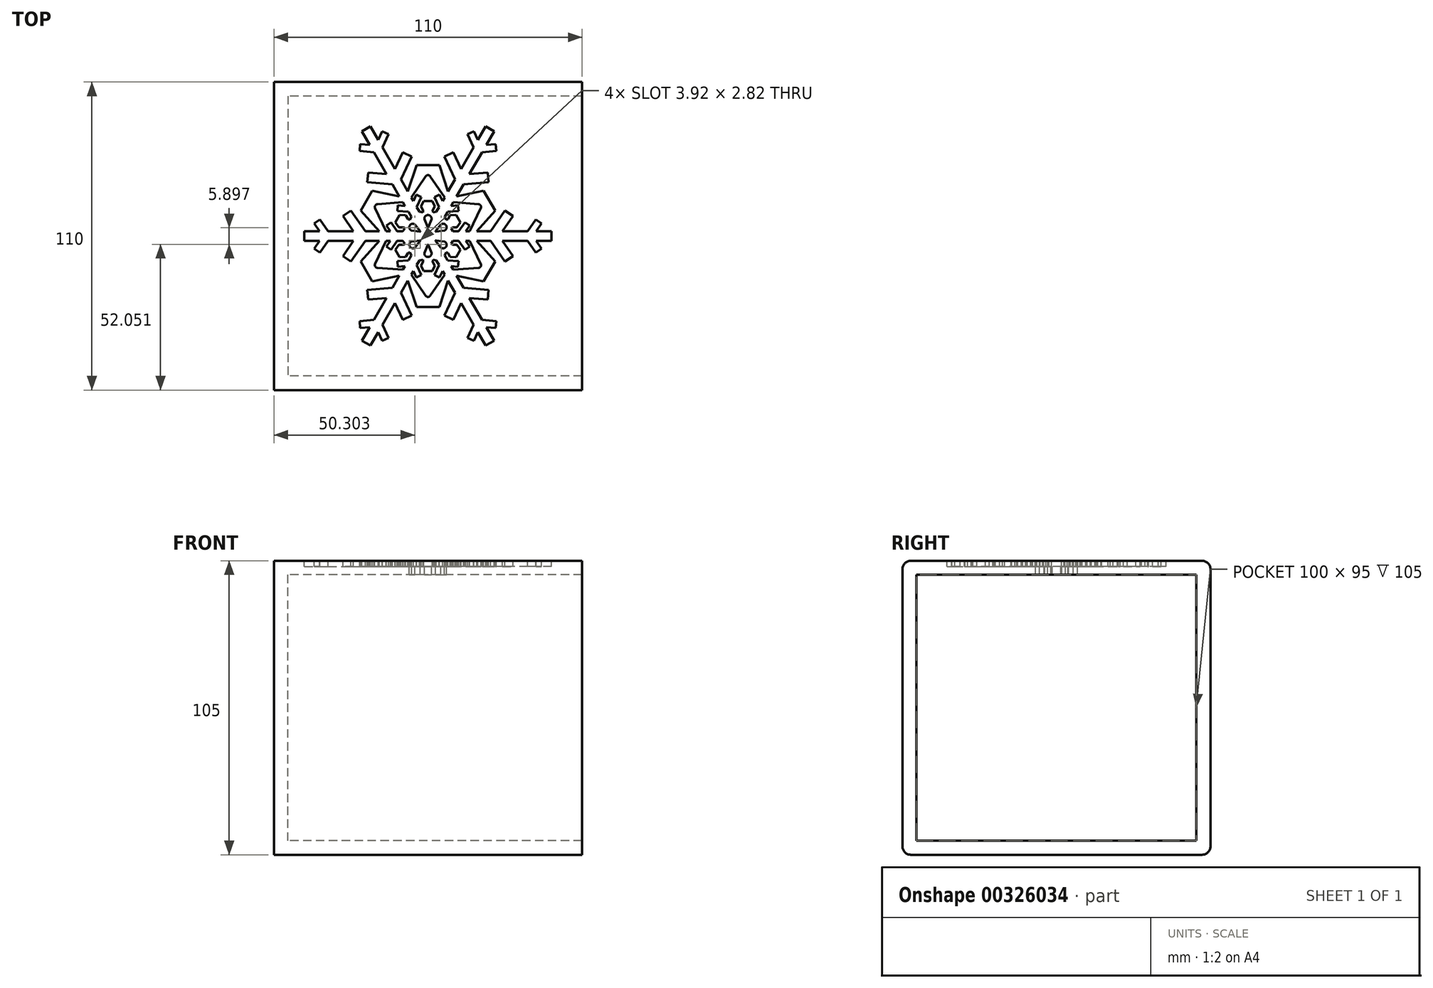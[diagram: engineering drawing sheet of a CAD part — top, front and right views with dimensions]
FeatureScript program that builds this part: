
annotation { "Feature Type Name" : "Feature", "Feature Type Description" : "" }
export const myFeature = defineFeature(function(context is Context, id is Id, definition is map)
    precondition{}
    {
        {
            var Q0;
            Q0=qCreatedBy(makeId("Top.planeOp"),FACE);
            var sketch = newSketch(context, id + "F0", { "sketchPlane" : qUnion([Q0])});
            skLineSegment(sketch, "E0.bottom", {"start": v(-43.7, 44.8) * mm, "end": v(41.1, 44.8) * mm});
            skLineSegment(sketch, "E0.top", {"start": v(-43.7, -40) * mm, "end": v(41.1, -40) * mm});
            skLineSegment(sketch, "E0.left", {"start": v(-43.7, 44.8) * mm, "end": v(-43.7, -40) * mm});
            skLineSegment(sketch, "E0.right", {"start": v(41.1, 44.8) * mm, "end": v(41.1, -40) * mm});
            skLineSegment(sketch, "E1", {"start": v(-44.15, 0) * mm, "end": v(-44.15, 1.75) * mm});
            skLineSegment(sketch, "E2", {"start": v(-44.15, 1.75) * mm, "end": v(-38.65, 1.75) * mm});
            skLineSegment(sketch, "E3", {"start": v(-38.65, 1.75) * mm, "end": v(-40.58, 4.5) * mm});
            skLineSegment(sketch, "E4", {"start": v(-40.58, 4.5) * mm, "end": v(-38.53, 5.94) * mm});
            skLineSegment(sketch, "E5", {"start": v(-38.53, 5.94) * mm, "end": v(-35.6, 1.75) * mm});
            skLineSegment(sketch, "E6", {"start": v(-35.6, 1.75) * mm, "end": v(-26.6, 1.75) * mm});
            skLineSegment(sketch, "E7", {"start": v(-26.6, 1.75) * mm, "end": v(-30.36, 7.13) * mm});
            skLineSegment(sketch, "E8", {"start": v(-30.36, 7.13) * mm, "end": v(-27.49, 9.13) * mm});
            skLineSegment(sketch, "E9", {"start": v(-27.49, 9.13) * mm, "end": v(-22.34, 1.75) * mm});
            skLineSegment(sketch, "E10", {"start": v(-22.34, 1.75) * mm, "end": v(-17.4, 1.75) * mm});
            skLineSegment(sketch, "E11", {"start": v(-14.94, 1.75) * mm, "end": v(-13.44, 1.75) * mm});
            skLineSegment(sketch, "E12", {"start": v(-13.44, 1.75) * mm, "end": v(-14.87, 3.8) * mm});
            skLineSegment(sketch, "E13", {"start": v(-14.87, 3.8) * mm, "end": v(-13.23, 4.94) * mm});
            skLineSegment(sketch, "E14", {"start": v(-13.23, 4.94) * mm, "end": v(-11, 1.75) * mm});
            skLineSegment(sketch, "E15", {"start": v(0, 0) * mm, "end": v(-44.15, 0) * mm, "construction": true});
            skLineSegment(sketch, "E16", {"start": v(-11, 1.75) * mm, "end": v(-8.98, 1.75) * mm});
            skLineSegment(sketch, "E17", {"start": v(0, 0) * mm, "end": v(-10.85, 6.27) * mm});
            skLineSegment(sketch, "E18", {"start": v(-8.98, 1.75) * mm, "end": v(-8.24, 2.67) * mm});
            skLineSegment(sketch, "E19", {"start": v(-8.24, 2.67) * mm, "end": v(-8.84, 3.15) * mm});
            skLineSegment(sketch, "E20", {"start": v(-8.84, 3.15) * mm, "end": v(-10.37, 3.15) * mm});
            skLineSegment(sketch, "E21", {"start": v(-10.37, 3.15) * mm, "end": v(-11.62, 4.94) * mm});
            skLineSegment(sketch, "E22", {"start": v(-11.62, 4.94) * mm, "end": v(-10.85, 6.27) * mm});
            skLineSegment(sketch, "E23", {"start": v(-10.85, 6.27) * mm, "end": v(-31.84, 18.38) * mm, "construction": true});
            skLineSegment(sketch, "E24", {"start": v(-23.98, 9.13) * mm, "end": v(-21.94, 12.67) * mm});
            skLineSegment(sketch, "E25", {"start": v(-14.94, 1.75) * mm, "end": v(-19.5, 11.26) * mm});
            skLineSegment(sketch, "E26", {"start": v(-23.98, 9.13) * mm, "end": v(-17.4, 1.75) * mm});
            skLineSegment(sketch, "E27", {"start": v(-21.94, 12.67) * mm, "end": v(-19.5, 11.26) * mm});
            skLineSegment(sketch, "E28.MirrorCS", {"start": v(0, 0) * mm, "end": v(-10.85, -6.27) * mm});
            skLineSegment(sketch, "E29.MirrorCS", {"start": v(-44.15, 0) * mm, "end": v(-44.15, -1.75) * mm});
            skLineSegment(sketch, "E30.MirrorCS", {"start": v(-14.94, -1.75) * mm, "end": v(-13.44, -1.75) * mm});
            skLineSegment(sketch, "E31.MirrorCS", {"start": v(-11.62, -4.94) * mm, "end": v(-10.85, -6.27) * mm});
            skLineSegment(sketch, "E32.MirrorCS", {"start": v(-14.87, -3.8) * mm, "end": v(-13.23, -4.94) * mm});
            skLineSegment(sketch, "E33.MirrorCS", {"start": v(-8.98, -1.75) * mm, "end": v(-8.24, -2.67) * mm});
            skLineSegment(sketch, "E34.MirrorCS", {"start": v(-8.84, -3.15) * mm, "end": v(-10.37, -3.15) * mm});
            skLineSegment(sketch, "E35.MirrorCS", {"start": v(-8.24, -2.67) * mm, "end": v(-8.84, -3.15) * mm});
            skLineSegment(sketch, "E36.MirrorCS", {"start": v(-14.94, -1.75) * mm, "end": v(-19.5, -11.26) * mm});
            skLineSegment(sketch, "E37.MirrorCS", {"start": v(-27.49, -9.13) * mm, "end": v(-22.34, -1.75) * mm});
            skLineSegment(sketch, "E38.MirrorCS", {"start": v(-21.94, -12.67) * mm, "end": v(-19.5, -11.26) * mm});
            skLineSegment(sketch, "E39.MirrorCS", {"start": v(-23.98, -9.13) * mm, "end": v(-21.94, -12.67) * mm});
            skLineSegment(sketch, "E40.MirrorCS", {"start": v(-11, -1.75) * mm, "end": v(-8.98, -1.75) * mm});
            skLineSegment(sketch, "E41.MirrorCS", {"start": v(-38.53, -5.94) * mm, "end": v(-35.6, -1.75) * mm});
            skLineSegment(sketch, "E42.MirrorCS", {"start": v(-40.58, -4.5) * mm, "end": v(-38.53, -5.94) * mm});
            skLineSegment(sketch, "E43.MirrorCS", {"start": v(-38.65, -1.75) * mm, "end": v(-40.58, -4.5) * mm});
            skLineSegment(sketch, "E44.MirrorCS", {"start": v(-44.15, -1.75) * mm, "end": v(-38.65, -1.75) * mm});
            skLineSegment(sketch, "E45.MirrorCS", {"start": v(-23.98, -9.13) * mm, "end": v(-17.4, -1.75) * mm});
            skLineSegment(sketch, "E46.MirrorCS", {"start": v(-30.36, -7.13) * mm, "end": v(-27.49, -9.13) * mm});
            skLineSegment(sketch, "E47.MirrorCS", {"start": v(-26.6, -1.75) * mm, "end": v(-30.36, -7.13) * mm});
            skLineSegment(sketch, "E48.MirrorCS", {"start": v(-35.6, -1.75) * mm, "end": v(-26.6, -1.75) * mm});
            skLineSegment(sketch, "E49.MirrorCS", {"start": v(-22.34, -1.75) * mm, "end": v(-17.4, -1.75) * mm});
            skLineSegment(sketch, "E50.MirrorCS", {"start": v(-13.44, -1.75) * mm, "end": v(-14.87, -3.8) * mm});
            skLineSegment(sketch, "E51.MirrorCS", {"start": v(-10.37, -3.15) * mm, "end": v(-11.62, -4.94) * mm});
            skLineSegment(sketch, "E52.MirrorCS", {"start": v(-13.23, -4.94) * mm, "end": v(-11, -1.75) * mm});
            skSolve(sketch);
        }
        {
            var Q0;
            Q0=makeQuery(id+"F0.imprint","IMPRINT",FACE,{"disambiguationData":[TD([[makeQuery(id+"F0.imprint","IMPRINT",EDGE,{"derivedFrom":sQuery(id+"F0.wireOp",EDGE,"E1")}),-1.0]])]});
            var Q1;
            {var subQ0=sQuery(id+"F0.wireOp",EDGE,"E3");Q1=makeQuery(id+"F0.imprint","IMPRINT",FACE,{"disambiguationData":[TD([[makeQuery(id+"F0.imprint","IMPRINT",EDGE,{"derivedFrom":subQ0}),-1.0]])]});}
            extrude(context, id + "F1", {"entities" : qUnion([Q0, Q1]), "endBound" : BoundingType.SYMMETRIC, "depth" : 3 * mm});
        }
        {
            var Q0;
            Q0=qCreatedBy(makeId("Right.planeOp"),FACE);
            var sketch = newSketch(context, id + "F2", { "sketchPlane" : qUnion([Q0])});
            skLineSegment(sketch, "E53", {"start": v(0, 0) * mm, "end": v(0, -43.45) * mm, "construction": true});
            skSolve(sketch);
        }
        {
            var Q0;
            Q0=makeQuery(id+"F1.opExtrude","SWEPT_BODY",BODY,{"disambiguationData":[OSD([sQuery(id+"F0.wireOp",EDGE,"E1"),sQuery(id+"F0.wireOp",EDGE,"E2"),sQuery(id+"F0.wireOp",EDGE,"E3"),sQuery(id+"F0.wireOp",EDGE,"E4"),sQuery(id+"F0.wireOp",EDGE,"E5"),sQuery(id+"F0.wireOp",EDGE,"E6"),sQuery(id+"F0.wireOp",EDGE,"E7"),sQuery(id+"F0.wireOp",EDGE,"E8"),sQuery(id+"F0.wireOp",EDGE,"E9"),sQuery(id+"F0.wireOp",EDGE,"E10"),sQuery(id+"F0.wireOp",EDGE,"189a7a4e-f39c-4bfd-b122-43a29ca94680"),sQuery(id+"F0.wireOp",EDGE,"67050dc1-3990-4a49-9707-dffdccfb30a0"),sQuery(id+"F0.wireOp",EDGE,"437a0215-fb6c-4063-ad75-b84b83856d58"),sQuery(id+"F0.wireOp",EDGE,"E11"),sQuery(id+"F0.wireOp",EDGE,"E12"),sQuery(id+"F0.wireOp",EDGE,"E13"),sQuery(id+"F0.wireOp",EDGE,"E14"),sQuery(id+"F0.wireOp",EDGE,"5e9898c1-a996-4e9f-834a-20b7154747a1"),sQuery(id+"F0.wireOp",EDGE,"4f175b08-8b9f-4015-be58-81c3dce13333"),sQuery(id+"F0.wireOp",EDGE,"3166d6ec-2b74-46b0-8a25-8ff819b97b050.MirrorCS"),sQuery(id+"F0.wireOp",EDGE,"3166d6ec-2b74-46b0-8a25-8ff819b97b051.MirrorCS"),sQuery(id+"F0.wireOp",EDGE,"3166d6ec-2b74-46b0-8a25-8ff819b97b052.MirrorCS"),sQuery(id+"F0.wireOp",EDGE,"3166d6ec-2b74-46b0-8a25-8ff819b97b053.MirrorCS"),sQuery(id+"F0.wireOp",EDGE,"3166d6ec-2b74-46b0-8a25-8ff819b97b054.MirrorCS"),sQuery(id+"F0.wireOp",EDGE,"3166d6ec-2b74-46b0-8a25-8ff819b97b055.MirrorCS"),sQuery(id+"F0.wireOp",EDGE,"3166d6ec-2b74-46b0-8a25-8ff819b97b056.MirrorCS"),sQuery(id+"F0.wireOp",EDGE,"3166d6ec-2b74-46b0-8a25-8ff819b97b057.MirrorCS"),sQuery(id+"F0.wireOp",EDGE,"3166d6ec-2b74-46b0-8a25-8ff819b97b058.MirrorCS"),sQuery(id+"F0.wireOp",EDGE,"3166d6ec-2b74-46b0-8a25-8ff819b97b059.MirrorCS"),sQuery(id+"F0.wireOp",EDGE,"3166d6ec-2b74-46b0-8a25-8ff819b97b0510.MirrorCS"),sQuery(id+"F0.wireOp",EDGE,"3166d6ec-2b74-46b0-8a25-8ff819b97b0511.MirrorCS"),sQuery(id+"F0.wireOp",EDGE,"3166d6ec-2b74-46b0-8a25-8ff819b97b0512.MirrorCS"),sQuery(id+"F0.wireOp",EDGE,"3166d6ec-2b74-46b0-8a25-8ff819b97b0513.MirrorCS"),sQuery(id+"F0.wireOp",EDGE,"3166d6ec-2b74-46b0-8a25-8ff819b97b0514.MirrorCS"),sQuery(id+"F0.wireOp",EDGE,"3166d6ec-2b74-46b0-8a25-8ff819b97b0515.MirrorCS"),sQuery(id+"F0.wireOp",EDGE,"3166d6ec-2b74-46b0-8a25-8ff819b97b0516.MirrorCS"),sQuery(id+"F0.wireOp",EDGE,"3166d6ec-2b74-46b0-8a25-8ff819b97b0517.MirrorCS"),sQuery(id+"F0.wireOp",EDGE,"3166d6ec-2b74-46b0-8a25-8ff819b97b0518.MirrorCS")])]});
            var Q1;
            Q1=sQuery(id+"F2.wireOp",EDGE,"E53");
            circularPattern(context, id + "F3", {"operationType" : NewBodyOperationType.ADD, "entities" : qUnion([Q0]), "axis" : qUnion([Q1]), "angle" : 60 * degree, "instanceCount" : 6});
        }
        {
            var Q0;
            {var subQ0=makeQuery(id+"F1.opExtrude","CAP_FACE",FACE,{"disambiguationData":[OSD([sQuery(id+"F0.wireOp",EDGE,"E1"),sQuery(id+"F0.wireOp",EDGE,"E2"),sQuery(id+"F0.wireOp",EDGE,"E3"),sQuery(id+"F0.wireOp",EDGE,"E4"),sQuery(id+"F0.wireOp",EDGE,"E5"),sQuery(id+"F0.wireOp",EDGE,"E6"),sQuery(id+"F0.wireOp",EDGE,"E7"),sQuery(id+"F0.wireOp",EDGE,"E8"),sQuery(id+"F0.wireOp",EDGE,"E9"),sQuery(id+"F0.wireOp",EDGE,"E10"),sQuery(id+"F0.wireOp",EDGE,"189a7a4e-f39c-4bfd-b122-43a29ca94680"),sQuery(id+"F0.wireOp",EDGE,"67050dc1-3990-4a49-9707-dffdccfb30a0"),sQuery(id+"F0.wireOp",EDGE,"437a0215-fb6c-4063-ad75-b84b83856d58"),sQuery(id+"F0.wireOp",EDGE,"E11"),sQuery(id+"F0.wireOp",EDGE,"E12"),sQuery(id+"F0.wireOp",EDGE,"E13"),sQuery(id+"F0.wireOp",EDGE,"E14"),sQuery(id+"F0.wireOp",EDGE,"E16"),sQuery(id+"F0.wireOp",EDGE,"E17"),sQuery(id+"F0.wireOp",EDGE,"E18"),sQuery(id+"F0.wireOp",EDGE,"E19"),sQuery(id+"F0.wireOp",EDGE,"E20"),sQuery(id+"F0.wireOp",EDGE,"E21"),sQuery(id+"F0.wireOp",EDGE,"E22"),sQuery(id+"F0.wireOp",EDGE,"0c32c283-354d-45ec-8926-575daeb4bd260.MirrorCS"),sQuery(id+"F0.wireOp",EDGE,"0c32c283-354d-45ec-8926-575daeb4bd261.MirrorCS"),sQuery(id+"F0.wireOp",EDGE,"0c32c283-354d-45ec-8926-575daeb4bd262.MirrorCS"),sQuery(id+"F0.wireOp",EDGE,"0c32c283-354d-45ec-8926-575daeb4bd263.MirrorCS"),sQuery(id+"F0.wireOp",EDGE,"0c32c283-354d-45ec-8926-575daeb4bd264.MirrorCS"),sQuery(id+"F0.wireOp",EDGE,"0c32c283-354d-45ec-8926-575daeb4bd265.MirrorCS"),sQuery(id+"F0.wireOp",EDGE,"0c32c283-354d-45ec-8926-575daeb4bd266.MirrorCS"),sQuery(id+"F0.wireOp",EDGE,"0c32c283-354d-45ec-8926-575daeb4bd267.MirrorCS"),sQuery(id+"F0.wireOp",EDGE,"0c32c283-354d-45ec-8926-575daeb4bd268.MirrorCS"),sQuery(id+"F0.wireOp",EDGE,"0c32c283-354d-45ec-8926-575daeb4bd269.MirrorCS"),sQuery(id+"F0.wireOp",EDGE,"0c32c283-354d-45ec-8926-575daeb4bd2610.MirrorCS"),sQuery(id+"F0.wireOp",EDGE,"0c32c283-354d-45ec-8926-575daeb4bd2611.MirrorCS"),sQuery(id+"F0.wireOp",EDGE,"0c32c283-354d-45ec-8926-575daeb4bd2612.MirrorCS"),sQuery(id+"F0.wireOp",EDGE,"0c32c283-354d-45ec-8926-575daeb4bd2613.MirrorCS"),sQuery(id+"F0.wireOp",EDGE,"0c32c283-354d-45ec-8926-575daeb4bd2614.MirrorCS"),sQuery(id+"F0.wireOp",EDGE,"0c32c283-354d-45ec-8926-575daeb4bd2615.MirrorCS"),sQuery(id+"F0.wireOp",EDGE,"0c32c283-354d-45ec-8926-575daeb4bd2616.MirrorCS"),sQuery(id+"F0.wireOp",EDGE,"0c32c283-354d-45ec-8926-575daeb4bd2617.MirrorCS"),sQuery(id+"F0.wireOp",EDGE,"0c32c283-354d-45ec-8926-575daeb4bd2618.MirrorCS"),sQuery(id+"F0.wireOp",EDGE,"0c32c283-354d-45ec-8926-575daeb4bd2619.MirrorCS"),sQuery(id+"F0.wireOp",EDGE,"0c32c283-354d-45ec-8926-575daeb4bd2620.MirrorCS"),sQuery(id+"F0.wireOp",EDGE,"0c32c283-354d-45ec-8926-575daeb4bd2621.MirrorCS"),sQuery(id+"F0.wireOp",EDGE,"0c32c283-354d-45ec-8926-575daeb4bd2622.MirrorCS"),sQuery(id+"F0.wireOp",EDGE,"0c32c283-354d-45ec-8926-575daeb4bd2623.MirrorCS")])],"isStart":false});Q0=makeQuery(id+"F3.boolean.opBoolean","MERGE",FACE,{"derivedFrom":[subQ0,makeQuery(id+"F3.opPattern","COPY",FACE,{"derivedFrom":subQ0,"instanceName":"1"}),makeQuery(id+"F3.opPattern","COPY",FACE,{"derivedFrom":subQ0,"instanceName":"2"}),makeQuery(id+"F3.opPattern","COPY",FACE,{"derivedFrom":subQ0,"instanceName":"3"}),makeQuery(id+"F3.opPattern","COPY",FACE,{"derivedFrom":subQ0,"instanceName":"4"}),makeQuery(id+"F3.opPattern","COPY",FACE,{"derivedFrom":subQ0,"instanceName":"5"})]});}
            var sketch = newSketch(context, id + "F4", { "sketchPlane" : qUnion([Q0])});
            skLineSegment(sketch, "E54", {"start": v(0, 0) * mm, "end": v(-10.85, 6.27) * mm, "construction": true});
            skLineSegment(sketch, "E55", {"start": v(-6.5, 3.75) * mm, "end": v(-2.6, 1.5) * mm, "construction": true});
            skLineSegment(sketch, "E56", {"start": v(-5.87, 1.94) * mm, "end": v(-2.6, 1.5) * mm});
            skLineSegment(sketch, "E57.MirrorCS", {"start": v(-4.62, 4.1) * mm, "end": v(-2.6, 1.5) * mm});
            skLineSegment(sketch, "E58", {"start": v(-5.87, 1.94) * mm, "end": v(-4.62, 4.1) * mm, "construction": true});
            skArc(sketch, "E59", {"start": v(-4.62, 4.1) * mm, "mid": v(-6.5, 3.75) * mm, "end": v(-5.87, 1.94) * mm});
            skSolve(sketch);
        }
        {
            var Q0;
            Q0=makeQuery(id+"F4.imprint","IMPRINT",FACE,{"disambiguationData":[TD([[makeQuery(id+"F4.imprint","IMPRINT",EDGE,{"derivedFrom":sQuery(id+"F4.wireOp",EDGE,"980073ca-cf30-472a-b92e-9ee7ff5da41c")}),1.0]])]});
            var Q1;
            Q1=makeQuery(id+"F4.imprint","IMPRINT",FACE,{"disambiguationData":[TD([[makeQuery(id+"F4.imprint","IMPRINT",EDGE,{"derivedFrom":sQuery(id+"F4.wireOp",EDGE,"E56")}),1.0]])]});
            extrude(context, id + "F5", {"entities" : qUnion([Q0, Q1]), "operationType" : NewBodyOperationType.REMOVE, "endBound" : BoundingType.UP_TO_NEXT, "oppositeDirection" : true, "depth" : 25 * mm});
        }
        {
            var Q0;
            Q0=makeQuery(id+"F5.boolean.opBoolean","COPY",EDGE,{"derivedFrom":makeQuery(id+"F5.opExtrude","SWEPT_EDGE",EDGE,{"disambiguationData":[OSD([sQuery(id+"F4.wireOp",EDGE,"E56"),sQuery(id+"F4.wireOp",EDGE,"E57.MirrorCS")])]})});
            fillet(context, id + "F6", {"entities" : qUnion([Q0]), "radius" : 0.1 * mm, "tangentPropagation" : true, "allowEdgeOverflow" : false});
        }
        {
            var Q0;
            Q0=makeQuery(id+"F5.boolean.opBoolean","COPY",FACE,{"derivedFrom":makeQuery(id+"F5.opExtrude","SWEPT_FACE",FACE,{"disambiguationData":[OSD([sQuery(id+"F4.wireOp",EDGE,"E59")])]})});
            var Q1;
            Q1=makeQuery(id+"F5.boolean.opBoolean","COPY",FACE,{"derivedFrom":makeQuery(id+"F5.opExtrude","SWEPT_FACE",FACE,{"disambiguationData":[OSD([sQuery(id+"F4.wireOp",EDGE,"E56")])]})});
            var Q2;
            Q2=makeQuery(id+"F5.boolean.opBoolean","COPY",FACE,{"derivedFrom":makeQuery(id+"F5.opExtrude","SWEPT_FACE",FACE,{"disambiguationData":[OSD([sQuery(id+"F4.wireOp",EDGE,"E57.MirrorCS")])]})});
            var Q3;
            Q3=makeQuery(id+"F6.opFillet","BLEND_FACE",FACE,{"disambiguationData":[OSD([sQuery(id+"F4.wireOp",EDGE,"E56"),sQuery(id+"F4.wireOp",EDGE,"E57.MirrorCS")])]});
            var Q4;
            Q4=sQuery(id+"F2.wireOp",EDGE,"E53");
            circularPattern(context, id + "F7", {"faces" : qUnion([Q0, Q1, Q2, Q3]), "axis" : qUnion([Q4]), "angle" : 60 * degree, "instanceCount" : 6, "patternType" : PatternType.FACE});
        }
        {
            var Q0;
            {var subQ0=makeQuery(id+"F1.opExtrude","CAP_FACE",FACE,{"disambiguationData":[OSD([sQuery(id+"F0.wireOp",EDGE,"E1"),sQuery(id+"F0.wireOp",EDGE,"E2"),sQuery(id+"F0.wireOp",EDGE,"E3"),sQuery(id+"F0.wireOp",EDGE,"E4"),sQuery(id+"F0.wireOp",EDGE,"E5"),sQuery(id+"F0.wireOp",EDGE,"E6"),sQuery(id+"F0.wireOp",EDGE,"E7"),sQuery(id+"F0.wireOp",EDGE,"E8"),sQuery(id+"F0.wireOp",EDGE,"E9"),sQuery(id+"F0.wireOp",EDGE,"E10"),sQuery(id+"F0.wireOp",EDGE,"189a7a4e-f39c-4bfd-b122-43a29ca94680"),sQuery(id+"F0.wireOp",EDGE,"67050dc1-3990-4a49-9707-dffdccfb30a0"),sQuery(id+"F0.wireOp",EDGE,"437a0215-fb6c-4063-ad75-b84b83856d58"),sQuery(id+"F0.wireOp",EDGE,"E11"),sQuery(id+"F0.wireOp",EDGE,"E12"),sQuery(id+"F0.wireOp",EDGE,"E13"),sQuery(id+"F0.wireOp",EDGE,"E14"),sQuery(id+"F0.wireOp",EDGE,"E16"),sQuery(id+"F0.wireOp",EDGE,"E17"),sQuery(id+"F0.wireOp",EDGE,"E18"),sQuery(id+"F0.wireOp",EDGE,"E19"),sQuery(id+"F0.wireOp",EDGE,"E20"),sQuery(id+"F0.wireOp",EDGE,"E21"),sQuery(id+"F0.wireOp",EDGE,"E22"),sQuery(id+"F0.wireOp",EDGE,"0c32c283-354d-45ec-8926-575daeb4bd260.MirrorCS"),sQuery(id+"F0.wireOp",EDGE,"0c32c283-354d-45ec-8926-575daeb4bd261.MirrorCS"),sQuery(id+"F0.wireOp",EDGE,"0c32c283-354d-45ec-8926-575daeb4bd262.MirrorCS"),sQuery(id+"F0.wireOp",EDGE,"0c32c283-354d-45ec-8926-575daeb4bd263.MirrorCS"),sQuery(id+"F0.wireOp",EDGE,"0c32c283-354d-45ec-8926-575daeb4bd264.MirrorCS"),sQuery(id+"F0.wireOp",EDGE,"0c32c283-354d-45ec-8926-575daeb4bd265.MirrorCS"),sQuery(id+"F0.wireOp",EDGE,"0c32c283-354d-45ec-8926-575daeb4bd266.MirrorCS"),sQuery(id+"F0.wireOp",EDGE,"0c32c283-354d-45ec-8926-575daeb4bd267.MirrorCS"),sQuery(id+"F0.wireOp",EDGE,"0c32c283-354d-45ec-8926-575daeb4bd268.MirrorCS"),sQuery(id+"F0.wireOp",EDGE,"0c32c283-354d-45ec-8926-575daeb4bd269.MirrorCS"),sQuery(id+"F0.wireOp",EDGE,"0c32c283-354d-45ec-8926-575daeb4bd2610.MirrorCS"),sQuery(id+"F0.wireOp",EDGE,"0c32c283-354d-45ec-8926-575daeb4bd2611.MirrorCS"),sQuery(id+"F0.wireOp",EDGE,"0c32c283-354d-45ec-8926-575daeb4bd2612.MirrorCS"),sQuery(id+"F0.wireOp",EDGE,"0c32c283-354d-45ec-8926-575daeb4bd2613.MirrorCS"),sQuery(id+"F0.wireOp",EDGE,"0c32c283-354d-45ec-8926-575daeb4bd2614.MirrorCS"),sQuery(id+"F0.wireOp",EDGE,"0c32c283-354d-45ec-8926-575daeb4bd2615.MirrorCS"),sQuery(id+"F0.wireOp",EDGE,"0c32c283-354d-45ec-8926-575daeb4bd2616.MirrorCS"),sQuery(id+"F0.wireOp",EDGE,"0c32c283-354d-45ec-8926-575daeb4bd2617.MirrorCS"),sQuery(id+"F0.wireOp",EDGE,"0c32c283-354d-45ec-8926-575daeb4bd2618.MirrorCS"),sQuery(id+"F0.wireOp",EDGE,"0c32c283-354d-45ec-8926-575daeb4bd2619.MirrorCS"),sQuery(id+"F0.wireOp",EDGE,"0c32c283-354d-45ec-8926-575daeb4bd2620.MirrorCS"),sQuery(id+"F0.wireOp",EDGE,"0c32c283-354d-45ec-8926-575daeb4bd2621.MirrorCS"),sQuery(id+"F0.wireOp",EDGE,"0c32c283-354d-45ec-8926-575daeb4bd2622.MirrorCS"),sQuery(id+"F0.wireOp",EDGE,"0c32c283-354d-45ec-8926-575daeb4bd2623.MirrorCS")])],"isStart":false});Q0=makeQuery(id+"F3.boolean.opBoolean","MERGE",FACE,{"derivedFrom":[subQ0,makeQuery(id+"F3.opPattern","COPY",FACE,{"derivedFrom":subQ0,"instanceName":"1"}),makeQuery(id+"F3.opPattern","COPY",FACE,{"derivedFrom":subQ0,"instanceName":"2"}),makeQuery(id+"F3.opPattern","COPY",FACE,{"derivedFrom":subQ0,"instanceName":"3"}),makeQuery(id+"F3.opPattern","COPY",FACE,{"derivedFrom":subQ0,"instanceName":"4"}),makeQuery(id+"F3.opPattern","COPY",FACE,{"derivedFrom":subQ0,"instanceName":"5"})]});}
            var sketch = newSketch(context, id + "F8", { "sketchPlane" : qUnion([Q0])});
            skArc(sketch, "E60", {"start": v(-44.15, 1.75) * mm, "mid": v(-51.75, 0) * mm, "end": v(-44.15, -1.75) * mm});
            skCircle(sketch, "E61", {"center": v(-47.75, 0) * mm, "radius": 2 * mm});
            skSolve(sketch);
        }
        {
            var Q0;
            Q0=makeQuery(id+"F8.imprint","IMPRINT",FACE,{"disambiguationData":[TD([[makeQuery(id+"F8.imprint","IMPRINT",EDGE,{"derivedFrom":sQuery(id+"F8.wireOp",EDGE,"E60")}),1.0]])]});
            extrude(context, id + "F9", {"entities" : qUnion([Q0]), "operationType" : NewBodyOperationType.ADD, "oppositeDirection" : true, "depth" : 3 * mm});
        }
        {
            var Q0;
            Q0=makeQuery(id+"F3.boolean.opBoolean","MERGE",EDGE,{"derivedFrom":[makeQuery(id+"F1.opExtrude","SWEPT_EDGE",EDGE,{"disambiguationData":[OSD([sQuery(id+"F0.wireOp",EDGE,"E25"),sQuery(id+"F0.wireOp",EDGE,"E27")])]}),makeQuery(id+"F3.opPattern","COPY",EDGE,{"derivedFrom":makeQuery(id+"F1.opExtrude","SWEPT_EDGE",EDGE,{"disambiguationData":[OSD([sQuery(id+"F0.wireOp",EDGE,"E36.MirrorCS"),sQuery(id+"F0.wireOp",EDGE,"E38.MirrorCS")])]}),"instanceName":"1"})]});
            var Q1;
            Q1=makeQuery(id+"F3.boolean.opBoolean","MERGE",EDGE,{"derivedFrom":[makeQuery(id+"F1.opExtrude","SWEPT_EDGE",EDGE,{"disambiguationData":[OSD([sQuery(id+"F0.wireOp",EDGE,"E36.MirrorCS"),sQuery(id+"F0.wireOp",EDGE,"E38.MirrorCS")])]}),makeQuery(id+"F3.opPattern","COPY",EDGE,{"derivedFrom":makeQuery(id+"F1.opExtrude","SWEPT_EDGE",EDGE,{"disambiguationData":[OSD([sQuery(id+"F0.wireOp",EDGE,"E25"),sQuery(id+"F0.wireOp",EDGE,"E27")])]}),"instanceName":"5"})]});
            var Q2;
            Q2=makeQuery(id+"F3.boolean.opBoolean","MERGE",EDGE,{"derivedFrom":[makeQuery(id+"F3.opPattern","COPY",EDGE,{"derivedFrom":makeQuery(id+"F1.opExtrude","SWEPT_EDGE",EDGE,{"disambiguationData":[OSD([sQuery(id+"F0.wireOp",EDGE,"E25"),sQuery(id+"F0.wireOp",EDGE,"E27")])]}),"instanceName":"4"}),makeQuery(id+"F3.opPattern","COPY",EDGE,{"derivedFrom":makeQuery(id+"F1.opExtrude","SWEPT_EDGE",EDGE,{"disambiguationData":[OSD([sQuery(id+"F0.wireOp",EDGE,"E36.MirrorCS"),sQuery(id+"F0.wireOp",EDGE,"E38.MirrorCS")])]}),"instanceName":"5"})]});
            var Q3;
            Q3=makeQuery(id+"F3.boolean.opBoolean","MERGE",EDGE,{"derivedFrom":[makeQuery(id+"F3.opPattern","COPY",EDGE,{"derivedFrom":makeQuery(id+"F1.opExtrude","SWEPT_EDGE",EDGE,{"disambiguationData":[OSD([sQuery(id+"F0.wireOp",EDGE,"E25"),sQuery(id+"F0.wireOp",EDGE,"E27")])]}),"instanceName":"3"}),makeQuery(id+"F3.opPattern","COPY",EDGE,{"derivedFrom":makeQuery(id+"F1.opExtrude","SWEPT_EDGE",EDGE,{"disambiguationData":[OSD([sQuery(id+"F0.wireOp",EDGE,"E36.MirrorCS"),sQuery(id+"F0.wireOp",EDGE,"E38.MirrorCS")])]}),"instanceName":"4"})]});
            var Q4;
            Q4=makeQuery(id+"F3.boolean.opBoolean","MERGE",EDGE,{"derivedFrom":[makeQuery(id+"F3.opPattern","COPY",EDGE,{"derivedFrom":makeQuery(id+"F1.opExtrude","SWEPT_EDGE",EDGE,{"disambiguationData":[OSD([sQuery(id+"F0.wireOp",EDGE,"E25"),sQuery(id+"F0.wireOp",EDGE,"E27")])]}),"instanceName":"1"}),makeQuery(id+"F3.opPattern","COPY",EDGE,{"derivedFrom":makeQuery(id+"F1.opExtrude","SWEPT_EDGE",EDGE,{"disambiguationData":[OSD([sQuery(id+"F0.wireOp",EDGE,"E36.MirrorCS"),sQuery(id+"F0.wireOp",EDGE,"E38.MirrorCS")])]}),"instanceName":"2"})]});
            var Q5;
            Q5=makeQuery(id+"F3.boolean.opBoolean","MERGE",EDGE,{"derivedFrom":[makeQuery(id+"F3.opPattern","COPY",EDGE,{"derivedFrom":makeQuery(id+"F1.opExtrude","SWEPT_EDGE",EDGE,{"disambiguationData":[OSD([sQuery(id+"F0.wireOp",EDGE,"E25"),sQuery(id+"F0.wireOp",EDGE,"E27")])]}),"instanceName":"2"}),makeQuery(id+"F3.opPattern","COPY",EDGE,{"derivedFrom":makeQuery(id+"F1.opExtrude","SWEPT_EDGE",EDGE,{"disambiguationData":[OSD([sQuery(id+"F0.wireOp",EDGE,"E36.MirrorCS"),sQuery(id+"F0.wireOp",EDGE,"E38.MirrorCS")])]}),"instanceName":"3"})]});
            fillet(context, id + "F10", {"entities" : qUnion([Q0, Q1, Q2, Q3, Q4, Q5]), "radius" : 1 * mm, "tangentPropagation" : true, "allowEdgeOverflow" : false});
        }
        {
            var Q0;
            {var subQ0=sQuery(id+"F0.wireOp",EDGE,"E29.MirrorCS");var subQ1=sQuery(id+"F0.wireOp",EDGE,"E1");var subQ2=makeQuery(id+"F1.opExtrude","CAP_FACE",FACE,{"disambiguationData":[OSD([subQ1,sQuery(id+"F0.wireOp",EDGE,"E2"),sQuery(id+"F0.wireOp",EDGE,"E3"),sQuery(id+"F0.wireOp",EDGE,"E4"),sQuery(id+"F0.wireOp",EDGE,"E5"),sQuery(id+"F0.wireOp",EDGE,"E6"),sQuery(id+"F0.wireOp",EDGE,"E7"),sQuery(id+"F0.wireOp",EDGE,"E8"),sQuery(id+"F0.wireOp",EDGE,"E9"),sQuery(id+"F0.wireOp",EDGE,"E10"),sQuery(id+"F0.wireOp",EDGE,"E11"),sQuery(id+"F0.wireOp",EDGE,"E12"),sQuery(id+"F0.wireOp",EDGE,"E13"),sQuery(id+"F0.wireOp",EDGE,"E14"),sQuery(id+"F0.wireOp",EDGE,"E16"),sQuery(id+"F0.wireOp",EDGE,"E17"),sQuery(id+"F0.wireOp",EDGE,"E18"),sQuery(id+"F0.wireOp",EDGE,"E19"),sQuery(id+"F0.wireOp",EDGE,"E20"),sQuery(id+"F0.wireOp",EDGE,"E21"),sQuery(id+"F0.wireOp",EDGE,"E22"),sQuery(id+"F0.wireOp",EDGE,"E24"),sQuery(id+"F0.wireOp",EDGE,"E25"),sQuery(id+"F0.wireOp",EDGE,"E26"),sQuery(id+"F0.wireOp",EDGE,"E27"),sQuery(id+"F0.wireOp",EDGE,"E28.MirrorCS"),subQ0,sQuery(id+"F0.wireOp",EDGE,"E30.MirrorCS"),sQuery(id+"F0.wireOp",EDGE,"E31.MirrorCS"),sQuery(id+"F0.wireOp",EDGE,"E32.MirrorCS"),sQuery(id+"F0.wireOp",EDGE,"E33.MirrorCS"),sQuery(id+"F0.wireOp",EDGE,"E34.MirrorCS"),sQuery(id+"F0.wireOp",EDGE,"E35.MirrorCS"),sQuery(id+"F0.wireOp",EDGE,"E36.MirrorCS"),sQuery(id+"F0.wireOp",EDGE,"E37.MirrorCS"),sQuery(id+"F0.wireOp",EDGE,"E38.MirrorCS"),sQuery(id+"F0.wireOp",EDGE,"E39.MirrorCS"),sQuery(id+"F0.wireOp",EDGE,"E40.MirrorCS"),sQuery(id+"F0.wireOp",EDGE,"E41.MirrorCS"),sQuery(id+"F0.wireOp",EDGE,"E42.MirrorCS"),sQuery(id+"F0.wireOp",EDGE,"E43.MirrorCS"),sQuery(id+"F0.wireOp",EDGE,"E44.MirrorCS"),sQuery(id+"F0.wireOp",EDGE,"E45.MirrorCS"),sQuery(id+"F0.wireOp",EDGE,"E46.MirrorCS"),sQuery(id+"F0.wireOp",EDGE,"E47.MirrorCS"),sQuery(id+"F0.wireOp",EDGE,"E48.MirrorCS"),sQuery(id+"F0.wireOp",EDGE,"E49.MirrorCS"),sQuery(id+"F0.wireOp",EDGE,"E50.MirrorCS"),sQuery(id+"F0.wireOp",EDGE,"E51.MirrorCS"),sQuery(id+"F0.wireOp",EDGE,"E52.MirrorCS")])],"isStart":false});Q0=makeQuery(id+"F9.boolean.opBoolean","MERGE",FACE,{"derivedFrom":[makeQuery(id+"F3.boolean.opBoolean","MERGE",FACE,{"derivedFrom":[subQ2,makeQuery(id+"F3.opPattern","COPY",FACE,{"derivedFrom":subQ2,"instanceName":"1"}),makeQuery(id+"F3.opPattern","COPY",FACE,{"derivedFrom":subQ2,"instanceName":"2"}),makeQuery(id+"F3.opPattern","COPY",FACE,{"derivedFrom":subQ2,"instanceName":"3"}),makeQuery(id+"F3.opPattern","COPY",FACE,{"derivedFrom":subQ2,"instanceName":"4"}),makeQuery(id+"F3.opPattern","COPY",FACE,{"derivedFrom":subQ2,"instanceName":"5"})]}),makeQuery(id+"F9.opExtrude","CAP_FACE",FACE,{"disambiguationData":[OSD([subQ1,subQ0,sQuery(id+"F8.wireOp",EDGE,"E60"),sQuery(id+"F8.wireOp",EDGE,"E61")])],"isStart":true})]});}
            var sketch = newSketch(context, id + "F11", { "sketchPlane" : qUnion([Q0])});
            skLineSegment(sketch, "E62", {"start": v(-44.15, 1.75) * mm, "end": v(-44.15, -1.75) * mm});
            skSolve(sketch);
        }
        {
            var Q0;
            Q0=makeQuery(id+"F11.imprint","IMPRINT",FACE,{"disambiguationData":[TD([[makeQuery(id+"F11.imprint","IMPRINT",EDGE,{"derivedFrom":sQuery(id+"F11.wireOp",EDGE,"E62")}),-1.0]])]});
            extrude(context, id + "F12", {"entities" : qUnion([Q0]), "operationType" : NewBodyOperationType.REMOVE, "oppositeDirection" : true, "depth" : 25 * mm});
        }
        {
            var Q0;
            {var subQ0=sQuery(id+"F0.wireOp",EDGE,"E29.MirrorCS");var subQ1=sQuery(id+"F0.wireOp",EDGE,"E1");var subQ2=makeQuery(id+"F1.opExtrude","CAP_FACE",FACE,{"disambiguationData":[OSD([subQ1,sQuery(id+"F0.wireOp",EDGE,"E2"),sQuery(id+"F0.wireOp",EDGE,"E3"),sQuery(id+"F0.wireOp",EDGE,"E4"),sQuery(id+"F0.wireOp",EDGE,"E5"),sQuery(id+"F0.wireOp",EDGE,"E6"),sQuery(id+"F0.wireOp",EDGE,"E7"),sQuery(id+"F0.wireOp",EDGE,"E8"),sQuery(id+"F0.wireOp",EDGE,"E9"),sQuery(id+"F0.wireOp",EDGE,"E10"),sQuery(id+"F0.wireOp",EDGE,"E11"),sQuery(id+"F0.wireOp",EDGE,"E12"),sQuery(id+"F0.wireOp",EDGE,"E13"),sQuery(id+"F0.wireOp",EDGE,"E14"),sQuery(id+"F0.wireOp",EDGE,"E16"),sQuery(id+"F0.wireOp",EDGE,"E17"),sQuery(id+"F0.wireOp",EDGE,"E18"),sQuery(id+"F0.wireOp",EDGE,"E19"),sQuery(id+"F0.wireOp",EDGE,"E20"),sQuery(id+"F0.wireOp",EDGE,"E21"),sQuery(id+"F0.wireOp",EDGE,"E22"),sQuery(id+"F0.wireOp",EDGE,"E24"),sQuery(id+"F0.wireOp",EDGE,"E25"),sQuery(id+"F0.wireOp",EDGE,"E26"),sQuery(id+"F0.wireOp",EDGE,"E27"),sQuery(id+"F0.wireOp",EDGE,"E28.MirrorCS"),subQ0,sQuery(id+"F0.wireOp",EDGE,"E30.MirrorCS"),sQuery(id+"F0.wireOp",EDGE,"E31.MirrorCS"),sQuery(id+"F0.wireOp",EDGE,"E32.MirrorCS"),sQuery(id+"F0.wireOp",EDGE,"E33.MirrorCS"),sQuery(id+"F0.wireOp",EDGE,"E34.MirrorCS"),sQuery(id+"F0.wireOp",EDGE,"E35.MirrorCS"),sQuery(id+"F0.wireOp",EDGE,"E36.MirrorCS"),sQuery(id+"F0.wireOp",EDGE,"E37.MirrorCS"),sQuery(id+"F0.wireOp",EDGE,"E38.MirrorCS"),sQuery(id+"F0.wireOp",EDGE,"E39.MirrorCS"),sQuery(id+"F0.wireOp",EDGE,"E40.MirrorCS"),sQuery(id+"F0.wireOp",EDGE,"E41.MirrorCS"),sQuery(id+"F0.wireOp",EDGE,"E42.MirrorCS"),sQuery(id+"F0.wireOp",EDGE,"E43.MirrorCS"),sQuery(id+"F0.wireOp",EDGE,"E44.MirrorCS"),sQuery(id+"F0.wireOp",EDGE,"E45.MirrorCS"),sQuery(id+"F0.wireOp",EDGE,"E46.MirrorCS"),sQuery(id+"F0.wireOp",EDGE,"E47.MirrorCS"),sQuery(id+"F0.wireOp",EDGE,"E48.MirrorCS"),sQuery(id+"F0.wireOp",EDGE,"E49.MirrorCS"),sQuery(id+"F0.wireOp",EDGE,"E50.MirrorCS"),sQuery(id+"F0.wireOp",EDGE,"E51.MirrorCS"),sQuery(id+"F0.wireOp",EDGE,"E52.MirrorCS")])],"isStart":true});Q0=makeQuery(id+"F9.boolean.opBoolean","MERGE",FACE,{"derivedFrom":[makeQuery(id+"F3.boolean.opBoolean","MERGE",FACE,{"derivedFrom":[subQ2,makeQuery(id+"F3.opPattern","COPY",FACE,{"derivedFrom":subQ2,"instanceName":"1"}),makeQuery(id+"F3.opPattern","COPY",FACE,{"derivedFrom":subQ2,"instanceName":"2"}),makeQuery(id+"F3.opPattern","COPY",FACE,{"derivedFrom":subQ2,"instanceName":"3"}),makeQuery(id+"F3.opPattern","COPY",FACE,{"derivedFrom":subQ2,"instanceName":"4"}),makeQuery(id+"F3.opPattern","COPY",FACE,{"derivedFrom":subQ2,"instanceName":"5"})]}),makeQuery(id+"F9.opExtrude","CAP_FACE",FACE,{"disambiguationData":[OSD([subQ1,subQ0,sQuery(id+"F8.wireOp",EDGE,"E60"),sQuery(id+"F8.wireOp",EDGE,"E61")])],"isStart":false})]});}
            var sketch = newSketch(context, id + "F13", { "sketchPlane" : qUnion([Q0])});
            skLineSegment(sketch, "E63.bottom", {"start": v(50, -50) * mm, "end": v(-50, -50) * mm});
            skLineSegment(sketch, "E63.top", {"start": v(50, 50) * mm, "end": v(-50, 50) * mm});
            skLineSegment(sketch, "E63.left", {"start": v(50, -50) * mm, "end": v(50, 50) * mm});
            skLineSegment(sketch, "E63.right", {"start": v(-50, -50) * mm, "end": v(-50, 50) * mm});
            skPoint(sketch, "E63.middle", {"position": v(0, 0) * mm});
            skLineSegment(sketch, "E64.0", {"start": v(55, 55) * mm, "end": v(-55, 55) * mm});
            skLineSegment(sketch, "E64.1", {"start": v(55, -55) * mm, "end": v(55, 55) * mm});
            skLineSegment(sketch, "E64.2", {"start": v(55, -55) * mm, "end": v(-55, -55) * mm});
            skLineSegment(sketch, "E64.3", {"start": v(-55, -55) * mm, "end": v(-55, 55) * mm});
            skSolve(sketch);
        }
        {
            var Q0;
            Q0=makeQuery(id+"F13.imprint","IMPRINT",FACE,{"disambiguationData":[TD([[makeQuery(id+"F13.imprint","IMPRINT",EDGE,{"derivedFrom":sQuery(id+"F13.wireOp",EDGE,"E63.bottom")}),-1.0]])]});
            var Q1;
            {var subQ11=sQuery(id+"F0.wireOp",EDGE,"E11");Q1=makeQuery(id+"F13.imprint","IMPRINT",FACE,{"disambiguationData":[TD([[makeQuery(id+"F13.imprint","IMPRINT",EDGE,{"derivedFrom":makeQuery(id+"F3.opPattern","COPY",EDGE,{"derivedFrom":makeQuery(id+"F1.opExtrude","CAP_EDGE",EDGE,{"disambiguationData":[OSD([subQ11])],"isStart":true}),"instanceName":"3"})}),-1.0]])]});}
            var Q2;
            {var subQ12=sQuery(id+"F0.wireOp",EDGE,"E11");Q2=makeQuery(id+"F13.imprint","IMPRINT",FACE,{"disambiguationData":[TD([[makeQuery(id+"F13.imprint","IMPRINT",EDGE,{"derivedFrom":makeQuery(id+"F3.opPattern","COPY",EDGE,{"derivedFrom":makeQuery(id+"F1.opExtrude","CAP_EDGE",EDGE,{"disambiguationData":[OSD([subQ12])],"isStart":true}),"instanceName":"2"})}),-1.0]])]});}
            var Q3;
            {var subQ13=sQuery(id+"F0.wireOp",EDGE,"E11");Q3=makeQuery(id+"F13.imprint","IMPRINT",FACE,{"disambiguationData":[TD([[makeQuery(id+"F13.imprint","IMPRINT",EDGE,{"derivedFrom":makeQuery(id+"F3.opPattern","COPY",EDGE,{"derivedFrom":makeQuery(id+"F1.opExtrude","CAP_EDGE",EDGE,{"disambiguationData":[OSD([subQ13])],"isStart":true}),"instanceName":"1"})}),-1.0]])]});}
            var Q4;
            {var subQ13=sQuery(id+"F0.wireOp",EDGE,"E11");Q4=makeQuery(id+"F13.imprint","IMPRINT",FACE,{"disambiguationData":[TD([[makeQuery(id+"F13.imprint","IMPRINT",EDGE,{"derivedFrom":makeQuery(id+"F3.opPattern","COPY",EDGE,{"derivedFrom":makeQuery(id+"F1.opExtrude","CAP_EDGE",EDGE,{"disambiguationData":[OSD([subQ13])],"isStart":true}),"instanceName":"4"})}),-1.0]])]});}
            var Q5;
            {var subQ10=sQuery(id+"F0.wireOp",EDGE,"E30.MirrorCS");Q5=makeQuery(id+"F13.imprint","IMPRINT",FACE,{"disambiguationData":[TD([[makeQuery(id+"F13.imprint","IMPRINT",EDGE,{"derivedFrom":makeQuery(id+"F1.opExtrude","CAP_EDGE",EDGE,{"disambiguationData":[OSD([subQ10])],"isStart":true})}),1.0]])]});}
            var Q6;
            {var subQ25=sQuery(id+"F0.wireOp",EDGE,"E11");Q6=makeQuery(id+"F13.imprint","IMPRINT",FACE,{"disambiguationData":[TD([[makeQuery(id+"F13.imprint","IMPRINT",EDGE,{"derivedFrom":makeQuery(id+"F1.opExtrude","CAP_EDGE",EDGE,{"disambiguationData":[OSD([subQ25])],"isStart":true})}),-1.0]])]});}
            var Q7;
            Q7=makeQuery(id+"F13.imprint","IMPRINT",FACE,{"disambiguationData":[TD([[makeQuery(id+"F13.imprint","IMPRINT",EDGE,{"derivedFrom":makeQuery(id+"F5.boolean.opBoolean","COPY",EDGE,{"derivedFrom":makeQuery(id+"F5.opExtrude","CAP_EDGE",EDGE,{"disambiguationData":[OSD([sQuery(id+"F4.wireOp",EDGE,"E59")])],"isStart":false})})}),1.0]])]});
            var Q8;
            Q8=makeQuery(id+"F13.imprint","IMPRINT",FACE,{"disambiguationData":[TD([[makeQuery(id+"F13.imprint","IMPRINT",EDGE,{"derivedFrom":makeQuery(id+"F7.opPattern","COPY",EDGE,{"derivedFrom":makeQuery(id+"F5.boolean.opBoolean","COPY",EDGE,{"derivedFrom":makeQuery(id+"F5.opExtrude","CAP_EDGE",EDGE,{"disambiguationData":[OSD([sQuery(id+"F4.wireOp",EDGE,"E59")])],"isStart":false})}),"instanceName":"1"})}),1.0]])]});
            var Q9;
            Q9=makeQuery(id+"F13.imprint","IMPRINT",FACE,{"disambiguationData":[TD([[makeQuery(id+"F13.imprint","IMPRINT",EDGE,{"derivedFrom":makeQuery(id+"F7.opPattern","COPY",EDGE,{"derivedFrom":makeQuery(id+"F5.boolean.opBoolean","COPY",EDGE,{"derivedFrom":makeQuery(id+"F5.opExtrude","CAP_EDGE",EDGE,{"disambiguationData":[OSD([sQuery(id+"F4.wireOp",EDGE,"E59")])],"isStart":false})}),"instanceName":"2"})}),1.0]])]});
            var Q10;
            Q10=makeQuery(id+"F13.imprint","IMPRINT",FACE,{"disambiguationData":[TD([[makeQuery(id+"F13.imprint","IMPRINT",EDGE,{"derivedFrom":makeQuery(id+"F7.opPattern","COPY",EDGE,{"derivedFrom":makeQuery(id+"F5.boolean.opBoolean","COPY",EDGE,{"derivedFrom":makeQuery(id+"F5.opExtrude","CAP_EDGE",EDGE,{"disambiguationData":[OSD([sQuery(id+"F4.wireOp",EDGE,"E59")])],"isStart":false})}),"instanceName":"3"})}),1.0]])]});
            var Q11;
            Q11=makeQuery(id+"F13.imprint","IMPRINT",FACE,{"disambiguationData":[TD([[makeQuery(id+"F13.imprint","IMPRINT",EDGE,{"derivedFrom":makeQuery(id+"F7.opPattern","COPY",EDGE,{"derivedFrom":makeQuery(id+"F5.boolean.opBoolean","COPY",EDGE,{"derivedFrom":makeQuery(id+"F5.opExtrude","CAP_EDGE",EDGE,{"disambiguationData":[OSD([sQuery(id+"F4.wireOp",EDGE,"E59")])],"isStart":false})}),"instanceName":"4"})}),1.0]])]});
            var Q12;
            Q12=makeQuery(id+"F13.imprint","IMPRINT",FACE,{"disambiguationData":[TD([[makeQuery(id+"F13.imprint","IMPRINT",EDGE,{"derivedFrom":makeQuery(id+"F7.opPattern","COPY",EDGE,{"derivedFrom":makeQuery(id+"F5.boolean.opBoolean","COPY",EDGE,{"derivedFrom":makeQuery(id+"F5.opExtrude","CAP_EDGE",EDGE,{"disambiguationData":[OSD([sQuery(id+"F4.wireOp",EDGE,"E59")])],"isStart":false})}),"instanceName":"5"})}),1.0]])]});
            var Q13;
            {var subQ4=sQuery(id+"F0.wireOp",EDGE,"E2");var subQ5=makeQuery(id+"F1.opExtrude","CAP_EDGE",EDGE,{"disambiguationData":[OSD([subQ4])],"isStart":true});Q13=makeQuery(id+"F13.imprint","IMPRINT",FACE,{"disambiguationData":[TD([[makeQuery(id+"F13.imprint","IMPRINT",EDGE,{"derivedFrom":subQ5}),1.0]])]});}
            extrude(context, id + "F14", {"entities" : qUnion([Q0, Q1, Q2, Q3, Q4, Q5, Q6, Q7, Q8, Q9, Q10, Q11, Q12, Q13]), "operationType" : NewBodyOperationType.ADD, "depth" : 5 * mm});
        }
        {
            var Q0;
            Q0=makeQuery(id+"F13.imprint","IMPRINT",FACE,{"disambiguationData":[TD([[makeQuery(id+"F13.imprint","IMPRINT",EDGE,{"derivedFrom":sQuery(id+"F13.wireOp",EDGE,"E63.bottom")}),1.0]])]});
            extrude(context, id + "F15", {"entities" : qUnion([Q0]), "operationType" : NewBodyOperationType.ADD, "depth" : 105 * mm});
        }
        {
            var Q0;
            Q0=makeQuery(id+"F15.opExtrude","CAP_FACE",FACE,{"disambiguationData":[OSD([sQuery(id+"F13.wireOp",EDGE,"E63.bottom"),sQuery(id+"F13.wireOp",EDGE,"E63.top"),sQuery(id+"F13.wireOp",EDGE,"E63.left"),sQuery(id+"F13.wireOp",EDGE,"E63.right"),sQuery(id+"F13.wireOp",EDGE,"E64.0"),sQuery(id+"F13.wireOp",EDGE,"E64.1"),sQuery(id+"F13.wireOp",EDGE,"E64.2"),sQuery(id+"F13.wireOp",EDGE,"E64.3")])],"isStart":false});
            var sketch = newSketch(context, id + "F16", { "sketchPlane" : qUnion([Q0])});
            skLineSegment(sketch, "E65.0", {"start": v(50, -50) * mm, "end": v(-50, -50) * mm});
            skLineSegment(sketch, "E66.0", {"start": v(50, -50) * mm, "end": v(50, 50) * mm});
            skLineSegment(sketch, "E67.0", {"start": v(-50, -50) * mm, "end": v(-50, 50) * mm});
            skLineSegment(sketch, "E68.0", {"start": v(50, 50) * mm, "end": v(-50, 50) * mm});
            skSolve(sketch);
        }
        {
            var Q0;
            Q0=makeQuery(id+"F16.imprint","IMPRINT",FACE,{"disambiguationData":[TD([[makeQuery(id+"F16.imprint","IMPRINT",EDGE,{"derivedFrom":sQuery(id+"F16.wireOp",EDGE,"E65.0")}),-1.0]])]});
            extrude(context, id + "F17", {"entities" : qUnion([Q0]), "operationType" : NewBodyOperationType.ADD, "oppositeDirection" : true, "depth" : 5 * mm});
        }
        {
            var Q0;
            Q0=makeQuery(id+"F15.opExtrude","SWEPT_FACE",FACE,{"disambiguationData":[OSD([sQuery(id+"F13.wireOp",EDGE,"E64.1")])]});
            var sketch = newSketch(context, id + "F18", { "sketchPlane" : qUnion([Q0])});
            skLineSegment(sketch, "E69.bottom", {"start": v(-55, -106.5) * mm, "end": v(55, -106.5) * mm});
            skLineSegment(sketch, "E69.top", {"start": v(-55, -1.5) * mm, "end": v(55, -1.5) * mm});
            skLineSegment(sketch, "E69.left", {"start": v(-55, -106.5) * mm, "end": v(-55, -1.5) * mm});
            skLineSegment(sketch, "E69.right", {"start": v(55, -106.5) * mm, "end": v(55, -1.5) * mm});
            skLineSegment(sketch, "E70.0", {"start": v(-50, -101.5) * mm, "end": v(50, -101.5) * mm});
            skLineSegment(sketch, "E70.1", {"start": v(-50, -101.5) * mm, "end": v(-50, -6.5) * mm});
            skLineSegment(sketch, "E70.2", {"start": v(-50, -6.5) * mm, "end": v(50, -6.5) * mm});
            skLineSegment(sketch, "E70.3", {"start": v(50, -101.5) * mm, "end": v(50, -6.5) * mm});
            skSolve(sketch);
        }
        {
            var Q0;
            Q0=makeQuery(id+"F18.imprint","IMPRINT",FACE,{"disambiguationData":[TD([[makeQuery(id+"F18.imprint","IMPRINT",EDGE,{"derivedFrom":sQuery(id+"F18.wireOp",EDGE,"E70.0")}),1.0]])]});
            extrude(context, id + "F19", {"entities" : qUnion([Q0]), "operationType" : NewBodyOperationType.REMOVE, "oppositeDirection" : true, "depth" : 10 * mm});
        }
        {
            var Q0;
            {var subQ0=sQuery(id+"F0.wireOp",EDGE,"E29.MirrorCS");var subQ1=sQuery(id+"F0.wireOp",EDGE,"E1");var subQ2=makeQuery(id+"F1.opExtrude","CAP_FACE",FACE,{"disambiguationData":[OSD([subQ1,sQuery(id+"F0.wireOp",EDGE,"E2"),sQuery(id+"F0.wireOp",EDGE,"E3"),sQuery(id+"F0.wireOp",EDGE,"E4"),sQuery(id+"F0.wireOp",EDGE,"E5"),sQuery(id+"F0.wireOp",EDGE,"E6"),sQuery(id+"F0.wireOp",EDGE,"E7"),sQuery(id+"F0.wireOp",EDGE,"E8"),sQuery(id+"F0.wireOp",EDGE,"E9"),sQuery(id+"F0.wireOp",EDGE,"E10"),sQuery(id+"F0.wireOp",EDGE,"E11"),sQuery(id+"F0.wireOp",EDGE,"E12"),sQuery(id+"F0.wireOp",EDGE,"E13"),sQuery(id+"F0.wireOp",EDGE,"E14"),sQuery(id+"F0.wireOp",EDGE,"E16"),sQuery(id+"F0.wireOp",EDGE,"E17"),sQuery(id+"F0.wireOp",EDGE,"E18"),sQuery(id+"F0.wireOp",EDGE,"E19"),sQuery(id+"F0.wireOp",EDGE,"E20"),sQuery(id+"F0.wireOp",EDGE,"E21"),sQuery(id+"F0.wireOp",EDGE,"E22"),sQuery(id+"F0.wireOp",EDGE,"E24"),sQuery(id+"F0.wireOp",EDGE,"E25"),sQuery(id+"F0.wireOp",EDGE,"E26"),sQuery(id+"F0.wireOp",EDGE,"E27"),sQuery(id+"F0.wireOp",EDGE,"E28.MirrorCS"),subQ0,sQuery(id+"F0.wireOp",EDGE,"E30.MirrorCS"),sQuery(id+"F0.wireOp",EDGE,"E31.MirrorCS"),sQuery(id+"F0.wireOp",EDGE,"E32.MirrorCS"),sQuery(id+"F0.wireOp",EDGE,"E33.MirrorCS"),sQuery(id+"F0.wireOp",EDGE,"E34.MirrorCS"),sQuery(id+"F0.wireOp",EDGE,"E35.MirrorCS"),sQuery(id+"F0.wireOp",EDGE,"E36.MirrorCS"),sQuery(id+"F0.wireOp",EDGE,"E37.MirrorCS"),sQuery(id+"F0.wireOp",EDGE,"E38.MirrorCS"),sQuery(id+"F0.wireOp",EDGE,"E39.MirrorCS"),sQuery(id+"F0.wireOp",EDGE,"E40.MirrorCS"),sQuery(id+"F0.wireOp",EDGE,"E41.MirrorCS"),sQuery(id+"F0.wireOp",EDGE,"E42.MirrorCS"),sQuery(id+"F0.wireOp",EDGE,"E43.MirrorCS"),sQuery(id+"F0.wireOp",EDGE,"E44.MirrorCS"),sQuery(id+"F0.wireOp",EDGE,"E45.MirrorCS"),sQuery(id+"F0.wireOp",EDGE,"E46.MirrorCS"),sQuery(id+"F0.wireOp",EDGE,"E47.MirrorCS"),sQuery(id+"F0.wireOp",EDGE,"E48.MirrorCS"),sQuery(id+"F0.wireOp",EDGE,"E49.MirrorCS"),sQuery(id+"F0.wireOp",EDGE,"E50.MirrorCS"),sQuery(id+"F0.wireOp",EDGE,"E51.MirrorCS"),sQuery(id+"F0.wireOp",EDGE,"E52.MirrorCS")])],"isStart":false});Q0=makeQuery(id+"F9.boolean.opBoolean","MERGE",FACE,{"derivedFrom":[makeQuery(id+"F3.boolean.opBoolean","MERGE",FACE,{"derivedFrom":[subQ2,makeQuery(id+"F3.opPattern","COPY",FACE,{"derivedFrom":subQ2,"instanceName":"1"}),makeQuery(id+"F3.opPattern","COPY",FACE,{"derivedFrom":subQ2,"instanceName":"2"}),makeQuery(id+"F3.opPattern","COPY",FACE,{"derivedFrom":subQ2,"instanceName":"3"}),makeQuery(id+"F3.opPattern","COPY",FACE,{"derivedFrom":subQ2,"instanceName":"4"}),makeQuery(id+"F3.opPattern","COPY",FACE,{"derivedFrom":subQ2,"instanceName":"5"})]}),makeQuery(id+"F9.opExtrude","CAP_FACE",FACE,{"disambiguationData":[OSD([subQ1,subQ0,sQuery(id+"F8.wireOp",EDGE,"E60"),sQuery(id+"F8.wireOp",EDGE,"E61")])],"isStart":true})]});}
            extrude(context, id + "F20", {"entities" : qUnion([Q0]), "operationType" : NewBodyOperationType.REMOVE, "oppositeDirection" : true, "depth" : 5 * mm});
        }
        {
            var Q0;
            Q0=makeQuery(id+"F15.opExtrude","CAP_EDGE",EDGE,{"disambiguationData":[OSD([sQuery(id+"F13.wireOp",EDGE,"E64.2")])],"isStart":true});
            var Q1;
            Q1=makeQuery(id+"F15.opExtrude","CAP_EDGE",EDGE,{"disambiguationData":[OSD([sQuery(id+"F13.wireOp",EDGE,"E64.2")])],"isStart":false});
            var Q2;
            Q2=makeQuery(id+"F15.opExtrude","CAP_EDGE",EDGE,{"disambiguationData":[OSD([sQuery(id+"F13.wireOp",EDGE,"E64.0")])],"isStart":true});
            var Q3;
            Q3=makeQuery(id+"F15.opExtrude","CAP_EDGE",EDGE,{"disambiguationData":[OSD([sQuery(id+"F13.wireOp",EDGE,"E64.0")])],"isStart":false});
            fillet(context, id + "F21", {"entities" : qUnion([Q0, Q1, Q2, Q3]), "radius" : 3 * mm, "tangentPropagation" : true, "allowEdgeOverflow" : false});
        }
    });
